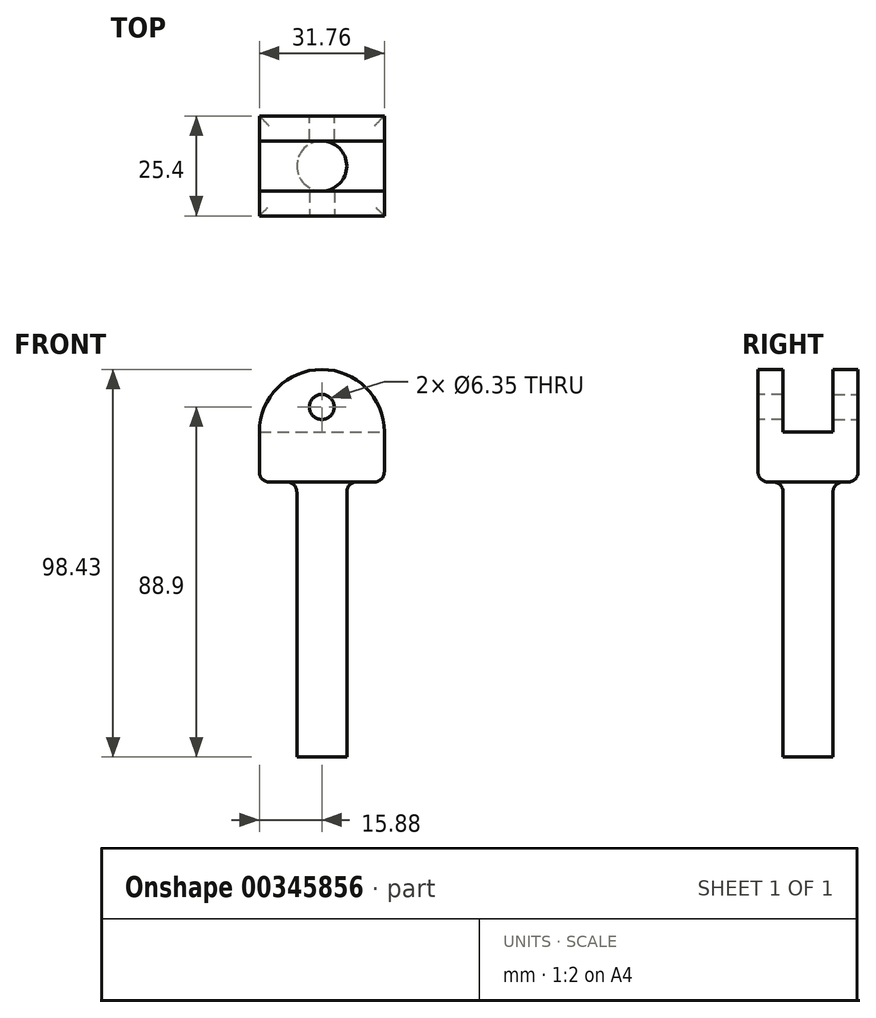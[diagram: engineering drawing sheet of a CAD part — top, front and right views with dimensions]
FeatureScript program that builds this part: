
annotation { "Feature Type Name" : "Feature", "Feature Type Description" : "" }
export const myFeature = defineFeature(function(context is Context, id is Id, definition is map)
    precondition{}
    {
        {
            var Q0;
            Q0=qCreatedBy(makeId("Front.planeOp"),FACE);
            var sketch = newSketch(context, id + "F6", { "sketchPlane" : qUnion([Q0])});
            skLineSegment(sketch, "E0.bottom", {"start": v(15.88, -6.35) * mm, "end": v(-15.88, -6.35) * mm});
            skLineSegment(sketch, "E0.top", {"start": v(-15.88, 6.35) * mm, "end": v(-15.88, 6.35) * mm});
            skLineSegment(sketch, "E0.left", {"start": v(15.88, -6.35) * mm, "end": v(15.88, 6.35) * mm});
            skLineSegment(sketch, "E0.right", {"start": v(-15.88, -6.35) * mm, "end": v(-15.88, 6.35) * mm});
            skPoint(sketch, "E0.middle", {"position": v(0, 0) * mm});
            skArc(sketch, "E1", {"start": v(15.88, 6.35) * mm, "mid": v(0, 22.23) * mm, "end": v(-15.88, 6.35) * mm});
            skCircle(sketch, "E2", {"center": v(0, 12.7) * mm, "radius": 3.18 * mm});
            skPoint(sketch, "E3.positionSnap0", {"position": v(0, -6.35) * mm});
            skLineSegment(sketch, "E4", {"start": v(-15.88, 6.35) * mm, "end": v(15.88, 6.35) * mm});
            skSolve(sketch);
        }
        {
            var Q0;
            Q0=makeQuery(id+"F6.imprint","IMPRINT",FACE,{"disambiguationData":[TD([[makeQuery(id+"F6.imprint","IMPRINT",EDGE,{"derivedFrom":sQuery(id+"F6.wireOp",EDGE,"E1")}),1.0]])]});
            extrude(context, id + "F0", {"entities" : qUnion([Q0]), "oppositeDirection" : true, "depth" : 6.35 * mm});
        }
        {
            var Q0;
            Q0=makeQuery(id+"F6.imprint","IMPRINT",FACE,{"disambiguationData":[TD([[makeQuery(id+"F6.imprint","IMPRINT",EDGE,{"derivedFrom":sQuery(id+"F6.wireOp",EDGE,"E0.bottom")}),-1.0]])]});
            extrude(context, id + "F1", {"entities" : qUnion([Q0]), "operationType" : NewBodyOperationType.ADD, "oppositeDirection" : true, "depth" : 12.7 * mm});
        }
        {
            var Q0;
            Q0=makeQuery(id+"F0.opExtrude","SWEPT_BODY",BODY,{"disambiguationData":[OSD([sQuery(id+"F6.wireOp",EDGE,"E1"),sQuery(id+"F6.wireOp",EDGE,"E2"),sQuery(id+"F6.wireOp",EDGE,"E4")])]});
            var Q1;
            Q1=makeQuery(id+"F1.opExtrude","CAP_FACE",FACE,{"disambiguationData":[OSD([sQuery(id+"F6.wireOp",EDGE,"E0.bottom"),sQuery(id+"F6.wireOp",EDGE,"E0.left"),sQuery(id+"F6.wireOp",EDGE,"E0.right"),sQuery(id+"F6.wireOp",EDGE,"E4")])],"isStart":false});
            mirror(context, id + "F2", {"operationType" : NewBodyOperationType.ADD, "entities" : qUnion([Q0]), "mirrorPlane" : qUnion([Q1])});
        }
        {
            var Q0;
            Q0=qCreatedBy(makeId("Top.planeOp"),FACE);
            var sketch = newSketch(context, id + "F3", { "sketchPlane" : qUnion([Q0])});
            skCircle(sketch, "E5", {"center": v(0, 12.7) * mm, "radius": 6.35 * mm});
            skSolve(sketch);
        }
        {
            var Q0;
            Q0=makeQuery(id+"F3.imprint","IMPRINT",FACE,{"disambiguationData":[TD([[makeQuery(id+"F3.imprint","IMPRINT",EDGE,{"derivedFrom":sQuery(id+"F3.wireOp",EDGE,"E5")}),1.0]])]});
            extrude(context, id + "F4", {"entities" : qUnion([Q0]), "operationType" : NewBodyOperationType.ADD, "oppositeDirection" : true, "depth" : 76.2 * mm});
        }
        {
            var Q0;
            {var subQ0=makeQuery(id+"F1.opExtrude","SWEPT_FACE",FACE,{"disambiguationData":[OSD([sQuery(id+"F6.wireOp",EDGE,"E0.bottom")])]});Q0=makeQuery(id+"F2.boolean.opBoolean","MERGE",FACE,{"derivedFrom":[subQ0,makeQuery(id+"F2.opPattern","COPY",FACE,{"derivedFrom":subQ0,"instanceName":"1"})]});}
            fillet(context, id + "F5", {"entities" : qUnion([Q0]), "radius" : 2.54 * mm, "tangentPropagation" : true, "allowEdgeOverflow" : false});
        }
    });
